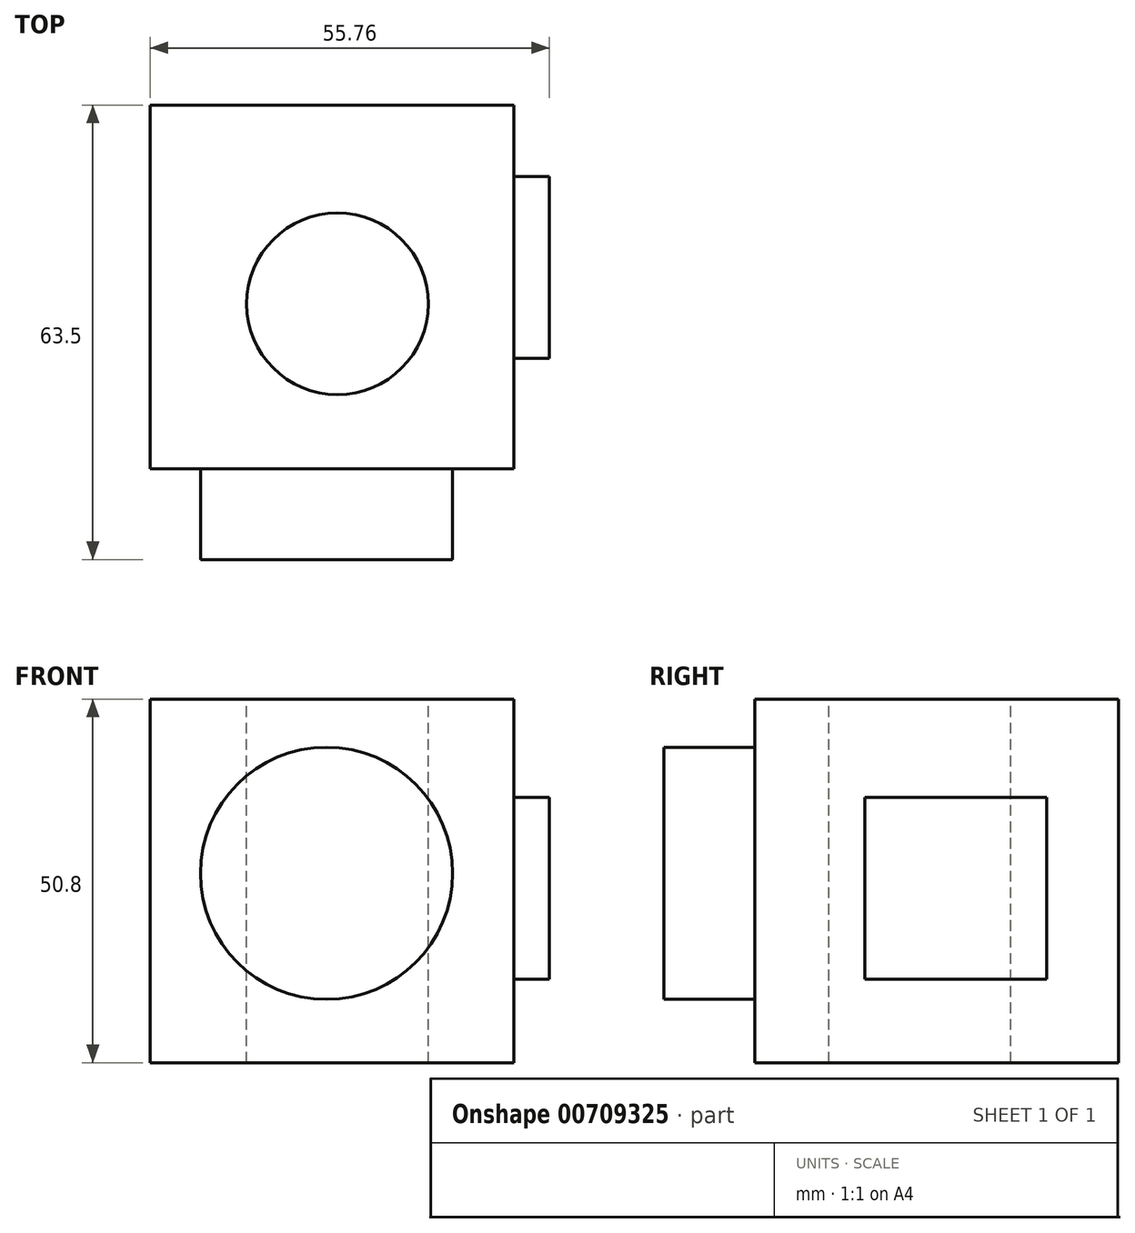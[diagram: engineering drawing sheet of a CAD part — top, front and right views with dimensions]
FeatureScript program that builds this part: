
annotation { "Feature Type Name" : "Feature", "Feature Type Description" : "" }
export const myFeature = defineFeature(function(context is Context, id is Id, definition is map)
    precondition{}
    {
        {
            var Q0;
            Q0=qCreatedBy(makeId("Front.planeOp"),FACE);
            var sketch = newSketch(context, id + "F0", { "sketchPlane" : qUnion([Q0])});
            skLineSegment(sketch, "E0", {"start": v(-43.06, 24.35) * mm, "end": v(7.74, 24.35) * mm});
            skLineSegment(sketch, "E1", {"start": v(7.74, 24.35) * mm, "end": v(7.74, -26.45) * mm});
            skLineSegment(sketch, "E2", {"start": v(7.74, -26.45) * mm, "end": v(-43.06, -26.45) * mm});
            skLineSegment(sketch, "E3", {"start": v(-43.06, -26.45) * mm, "end": v(-43.06, 24.35) * mm});
            skSolve(sketch);
        }
        {
            var Q0;
            Q0=makeQuery(id+"F0.imprint","IMPRINT",FACE,{"disambiguationData":[TD([[makeQuery(id+"F0.imprint","IMPRINT",EDGE,{"derivedFrom":sQuery(id+"F0.wireOp",EDGE,"E0")}),-1.0]])]});
            extrude(context, id + "F1", {"entities" : qUnion([Q0]), "depth" : 50.8 * mm, "offsetDistance" : 25.4 * mm});
        }
        {
            var Q0;
            Q0=makeQuery(id+"F1.opExtrude","SWEPT_FACE",FACE,{"disambiguationData":[OSD([sQuery(id+"F0.wireOp",EDGE,"E0")])]});
            var sketch = newSketch(context, id + "F2", { "sketchPlane" : qUnion([Q0])});
            skCircle(sketch, "E4", {"center": v(-16.9, -27.78) * mm, "radius": 12.7 * mm});
            skSolve(sketch);
        }
        {
            var Q0;
            Q0=makeQuery(id+"F2.imprint","IMPRINT",FACE,{"disambiguationData":[TD([[makeQuery(id+"F2.imprint","IMPRINT",EDGE,{"derivedFrom":sQuery(id+"F2.wireOp",EDGE,"E4")}),1.0]])]});
            extrude(context, id + "F3", {"entities" : qUnion([Q0]), "operationType" : NewBodyOperationType.REMOVE, "oppositeDirection" : true, "depth" : 50.8 * mm, "offsetDistance" : 25.4 * mm});
        }
        {
            var Q0;
            Q0=qCreatedBy(makeId("Right.planeOp"),FACE);
            var sketch = newSketch(context, id + "F4", { "sketchPlane" : qUnion([Q0])});
            skLineSegment(sketch, "E5", {"start": v(-10.02, 10.6) * mm, "end": v(-10.02, -14.8) * mm});
            skLineSegment(sketch, "E6", {"start": v(-10.02, -14.8) * mm, "end": v(-35.42, -14.8) * mm});
            skLineSegment(sketch, "E7", {"start": v(-35.42, -14.8) * mm, "end": v(-35.42, 10.6) * mm});
            skLineSegment(sketch, "E8", {"start": v(-35.42, 10.6) * mm, "end": v(-10.02, 10.6) * mm});
            skSolve(sketch);
        }
        {
            var Q0;
            Q0 = qSketchRegion(id + "F4", true);
            extrude(context, id + "F5", {"entities" : qUnion([Q0]), "operationType" : NewBodyOperationType.ADD, "depth" : 12.7 * mm, "offsetDistance" : 25.4 * mm});
        }
        {
            var Q0;
            Q0=makeQuery(id+"F1.opExtrude","CAP_FACE",FACE,{"disambiguationData":[OSD([sQuery(id+"F0.wireOp",EDGE,"E0"),sQuery(id+"F0.wireOp",EDGE,"E1"),sQuery(id+"F0.wireOp",EDGE,"E2"),sQuery(id+"F0.wireOp",EDGE,"E3")])],"isStart":false});
            var sketch = newSketch(context, id + "F6", { "sketchPlane" : qUnion([Q0])});
            skCircle(sketch, "E9", {"center": v(-18.43, 0) * mm, "radius": 17.61 * mm});
            skSolve(sketch);
        }
        {
            var Q0;
            Q0=makeQuery(id+"F6.imprint","IMPRINT",FACE,{"disambiguationData":[TD([[makeQuery(id+"F6.imprint","IMPRINT",EDGE,{"derivedFrom":sQuery(id+"F6.wireOp",EDGE,"E9")}),1.0]])]});
            extrude(context, id + "F7", {"entities" : qUnion([Q0]), "operationType" : NewBodyOperationType.ADD, "depth" : 12.7 * mm, "offsetDistance" : 25.4 * mm});
        }
    });
